# Revit family: NX_Specialty_Switch
name_source: partatom
category: Electrical Equipment
units: mm (PartAtom-declared; Revit-internal decimal feet)

## family parameters
Cut with Voids When Loaded = No
Host = Face
OmniClass Number = 23.80.30.11.11
OmniClass Title = Main Switches
Part Type = Equipment Switch
Room Calculation Point = No
Round Connector Dimension = Use Diameter
Shared = No

## types (1)
- NX
    Apparent Load = 0.000 VA
    Assembly Code = D5020120
    Connector Description 1 = Power Supply
    Construction = Housing - Rugged, high impact, injection molded plastic
    Default Elevation = 48 "
    Description = Specialty Switch Stations
    Device Material = Plastic - White
    Load Classification = Power
    Manufacturer = NX Lighting Controls
    Model = NX Specialty Switches
    Operating Environment = Indoor use only
    Operating Temperature = 32° to 104° [0° to 40°]
    Power Factor = 1
    Power Requirements = Powered by NX™ SmartPORT using plenum rated CAT5 cables
    Relative Humidity = 0 to 95%
    Type Comments = Electrical Equipment
    URL = https://www.currentlighting.com
    Voltage = 120V
    Warranty = Five-year limited
    Weight = 0 kg

## geometry (parser evidence)
native form markers: Sweep x9
no freeform markers — native parametric forms only
